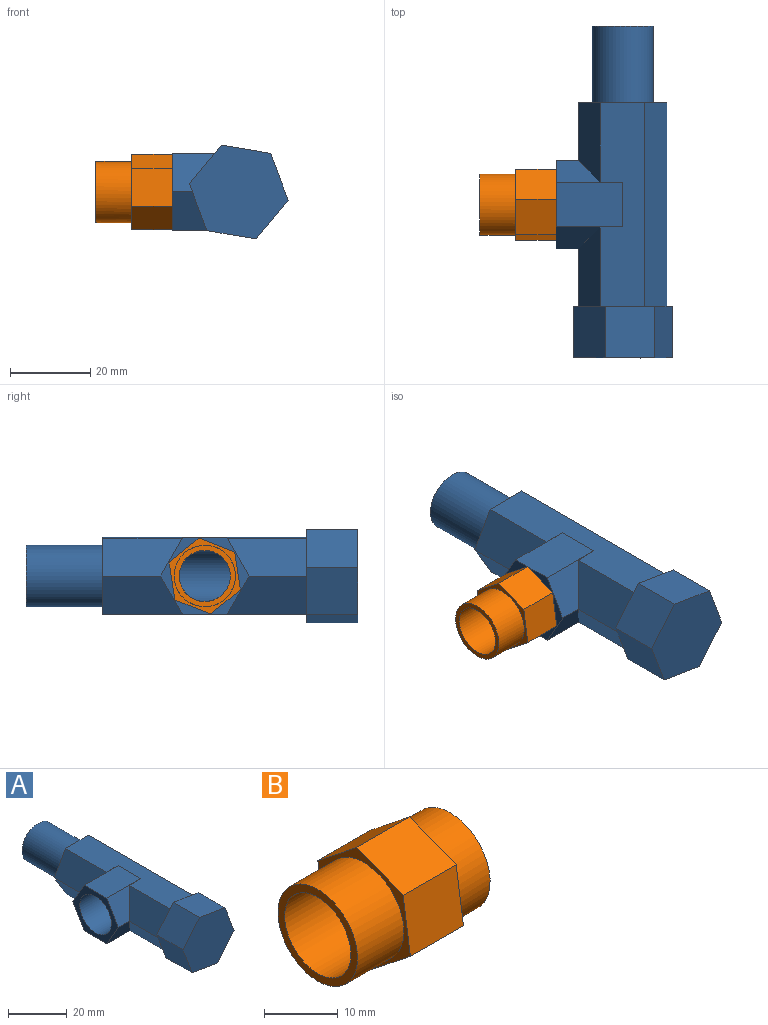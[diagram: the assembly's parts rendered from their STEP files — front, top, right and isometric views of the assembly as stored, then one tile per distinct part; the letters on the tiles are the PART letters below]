
ASSEMBLY  parts=2 mates=1
PART A: 30 faces, bbox 28.8x82.6x23.4 mm
  f0: cylinder r=6.35mm len=70.36mm, axis (0,1,0), area 2557.6mm2, adj f25,f26,f27,f28,f29
  f1: plane 50.8x9.44mm, normal (-0.86,0,-0.51), area 380.1mm2, adj f3,f4,f5,f8,f10,f11,f12,f23
  f2: plane 50.8x11mm, normal (-0.02,0,1), area 497.1mm2, adj f3,f4,f7,f8,f9,f13,f14,f23
  f3: plane 19.85x9.61mm, normal (-0.87,0,0.49), area 187.8mm2, adj f1,f2,f9,f10,f23
  f4: plane 19.85x9.61mm, normal (-0.87,0,0.49), area 187.8mm2, adj f1,f2,f8,f12,f13
  f5: plane 50.8x11mm, normal (0.02,0,-1), area 558.7mm2, adj f1,f6,f8,f23
  f6: plane 50.8x9.61mm, normal (0.87,0,-0.49), area 558.7mm2, adj f5,f7,f8,f23
  f7: plane 50.8x9.44mm, normal (0.86,0,0.51), area 558.7mm2, adj f2,f6,f8,f23
  f8: plane 21.99x19.22mm, normal (0,1,0), area 131.9mm2, adj f1,f2,f4,f5,f6,f7,f24
  f9: plane 16.43x9.53mm, normal (0,-0.87,0.5), area 91.1mm2, adj f2,f3,f10,f14,f15
  f10: plane 11.11x9.53mm, normal (0,-0.87,-0.5), area 90.9mm2, adj f1,f3,f9,f11,f15
  f11: plane 11.11x11mm, normal (0,0,-1), area 122.2mm2, adj f1,f10,f12,f15
  f12: plane 11.11x9.53mm, normal (0,0.87,-0.5), area 90.9mm2, adj f1,f4,f11,f13,f15
  f13: plane 16.43x9.53mm, normal (0,0.87,0.5), area 91.1mm2, adj f2,f4,f12,f14,f15
  f14: plane 16.43x11mm, normal (0,0,1), area 180.7mm2, adj f2,f9,f13,f15
  f15: plane 22x19.05mm, normal (-1,0,0), area 131.9mm2, adj f9,f10,f11,f12,f13,f14,f27
  f16: plane 12.7x11.68mm, normal (-0.94,0,-0.35), area 158.3mm2, adj f17,f21,f22,f23
  f17: plane 12.7x12.29mm, normal (-0.17,0,-0.99), area 158.3mm2, adj f16,f18,f22,f23
  f18: plane 12.7x9.61mm, normal (0.77,0,-0.64), area 158.3mm2, adj f17,f19,f22,f23
  f19: plane 12.7x11.68mm, normal (0.94,0,0.35), area 158.3mm2, adj f18,f20,f22,f23
  f20: plane 12.7x12.29mm, normal (0.17,0,0.99), area 158.3mm2, adj f19,f21,f22,f23
  f21: plane 12.7x9.61mm, normal (-0.77,0,0.64), area 158.3mm2, adj f16,f20,f22,f23
  f22: plane 24.59x23.36mm, normal (0,-1,0), area 403.7mm2, adj f16,f17,f18,f19,f20,f21
  f23: plane 24.59x23.36mm, normal (0,1,0), area 89.4mm2, adj f1,f2,f3,f5,f6,f7,f16,f17
  f24: cylinder r=7.62mm len=19.05mm, axis (0,-1,0), area 912.1mm2, adj f8,f25
  f25: plane 15.24x15.24mm, normal (0,1,0), area 55.7mm2, adj f0,f24
  f26: plane 12.7x12.7mm, normal (0,1,0), area 126.7mm2, adj f0
  f27: cylinder r=7.62mm len=17.02mm, axis (-1,0,0), area 657.1mm2, adj f0,f15,f28,f29
  f28: plane 8.49x1.29mm, normal (-1,0,0), area 7.4mm2, adj f0,f27
  f29: plane 8.49x1.29mm, normal (-1,0,0), area 7.4mm2, adj f0,f27
PART B: 13 faces, bbox 25.4x17.7x18.9 mm
  f0: plane 10.16x9.43mm, normal (0,-0.99,0.15), area 96.8mm2, adj f1,f5,f6,f7
  f1: plane 10.16x7.46mm, normal (0,-0.62,-0.78), area 96.8mm2, adj f0,f2,f6,f7
  f2: plane 10.16x8.87mm, normal (0,0.37,-0.93), area 96.8mm2, adj f1,f3,f6,f7
  f3: plane 10.16x9.43mm, normal (0,0.99,-0.15), area 96.8mm2, adj f2,f4,f6,f7
  f4: plane 10.16x7.46mm, normal (0,0.62,0.78), area 96.8mm2, adj f3,f5,f6,f7
  f5: plane 10.16x8.87mm, normal (0,-0.37,0.93), area 96.8mm2, adj f0,f4,f6,f7
  f6: plane 18.85x17.74mm, normal (1,0,0), area 53.6mm2, adj f0,f1,f2,f3,f4,f5,f10
  f7: plane 18.85x17.74mm, normal (-1,0,0), area 53.6mm2, adj f0,f1,f2,f3,f4,f5,f9
  f8: plane 15.24x15.24mm, normal (-1,0,0), area 55.7mm2, adj f9,f12
  f9: cylinder r=7.62mm len=15.24mm, axis (-1,0,0), area 425.6mm2, adj f7,f8
  f10: cylinder r=7.62mm len=15.24mm, axis (-1,0,0), area 304mm2, adj f6,f11
  f11: plane 15.24x15.24mm, normal (1,0,0), area 55.7mm2, adj f10,f12
  f12: cylinder r=6.35mm len=25.4mm, axis (-1,0,0), area 1013.4mm2, adj f8,f11
PLACE A t=(0.31,15.47,-8.57)mm
PLACE B t=(-26.36,-9.93,-8.57)mm
MATE fastened B.f9 <-> A.f27  axis (-1,0,0) through (-16.2,-9.93,-8.57)mm
